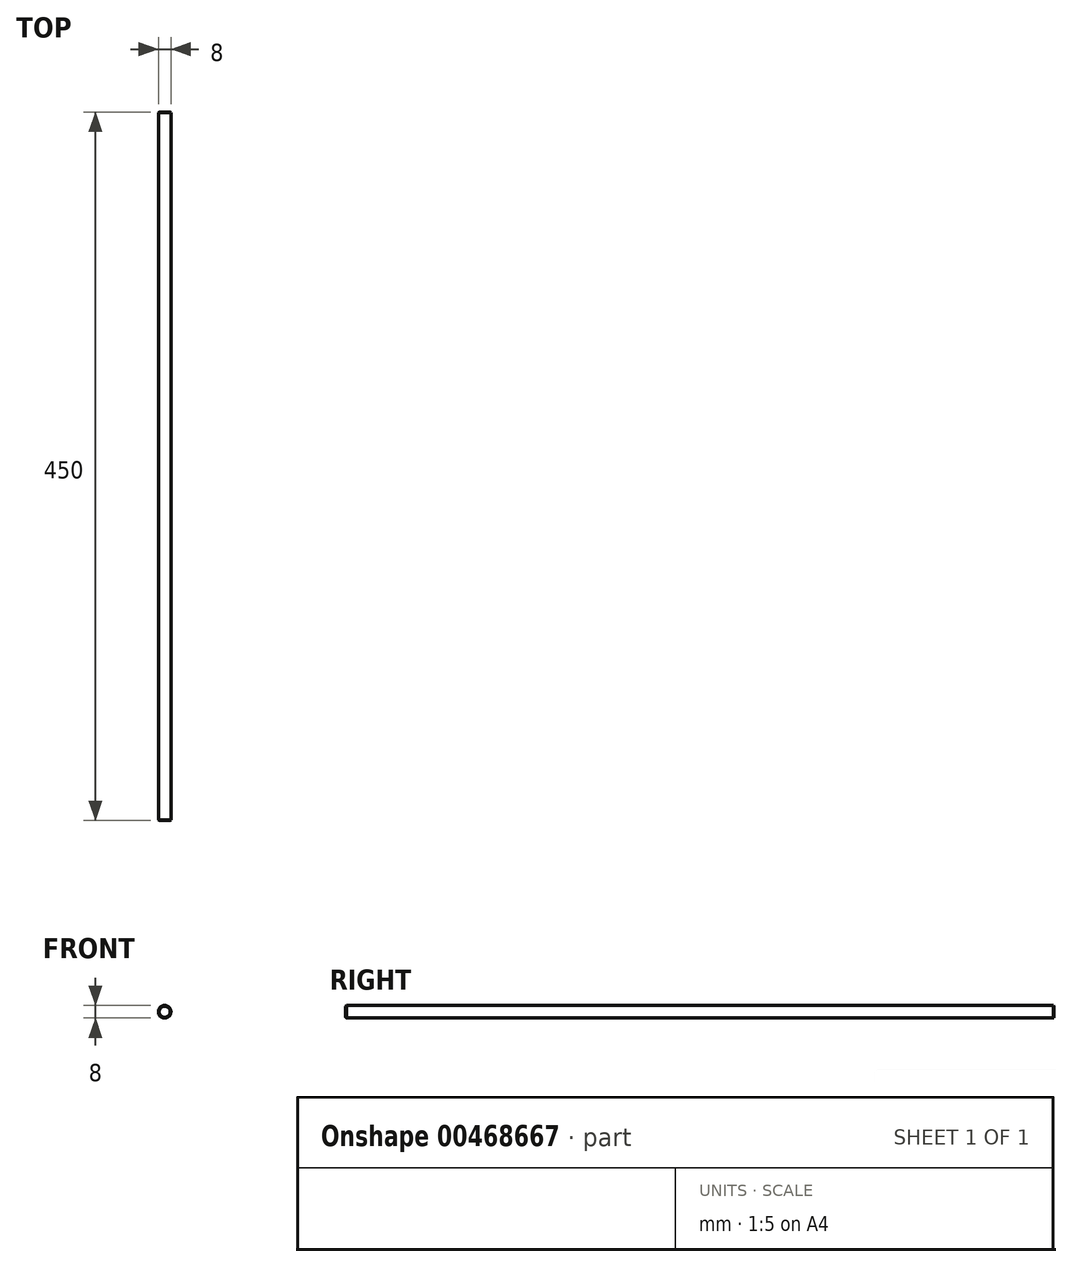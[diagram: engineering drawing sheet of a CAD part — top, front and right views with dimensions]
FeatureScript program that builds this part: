
annotation { "Feature Type Name" : "Feature", "Feature Type Description" : "" }
export const myFeature = defineFeature(function(context is Context, id is Id, definition is map)
    precondition{}
    {
        {
            var Q0;
            Q0=qCreatedBy(makeId("Front.planeOp"),FACE);
            var sketch = newSketch(context, id + "F0", { "sketchPlane" : qUnion([Q0])});
            skCircle(sketch, "E0", {"center": v(0, 0) * mm, "radius": 4 * mm});
            skSolve(sketch);
        }
        {
            var Q0;
            Q0=qSketchRegion(id+"F0",true);
            extrude(context, id + "F1", {"entities" : qUnion([Q0]), "depth" : 450 * mm, "offsetDistance" : 25 * mm});
        }
        {
            var Q0;
            Q0=makeQuery(id+"F1.opExtrude","CAP_EDGE",EDGE,{"disambiguationData":[OSD([sQuery(id+"F0.wireOp",EDGE,"E0")])],"isStart":false});
            var Q1;
            Q1=makeQuery(id+"F1.opExtrude","CAP_EDGE",EDGE,{"disambiguationData":[OSD([sQuery(id+"F0.wireOp",EDGE,"E0")])],"isStart":true});
            chamfer(context, id + "F2", {"entities" : qUnion([Q0, Q1]), "width" : 0.5 * mm, "tangentPropagation" : true});
        }
    });
